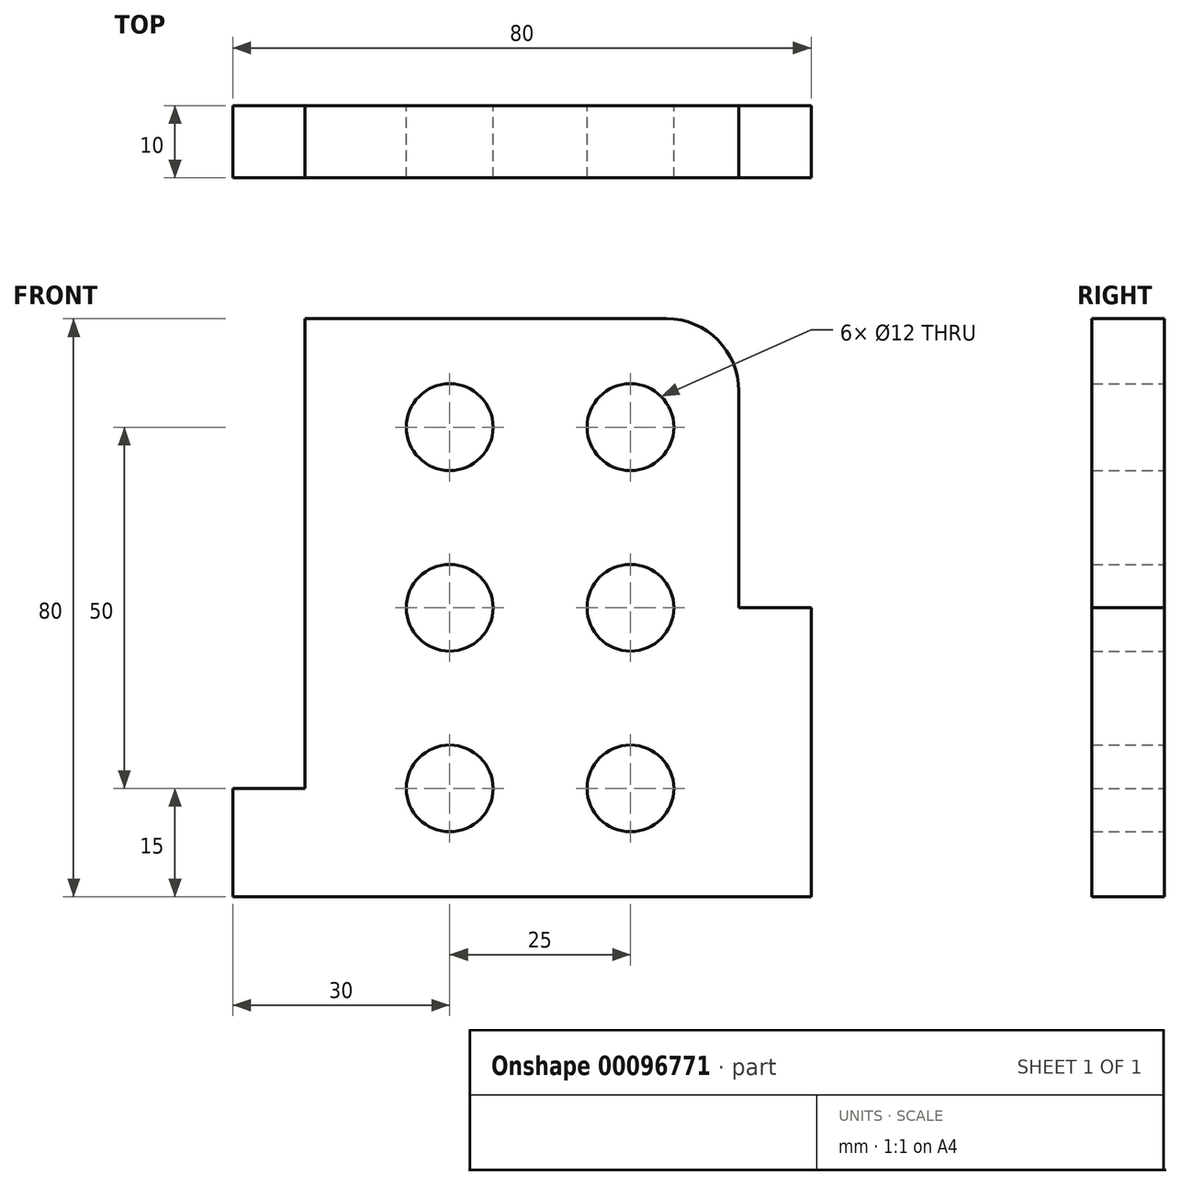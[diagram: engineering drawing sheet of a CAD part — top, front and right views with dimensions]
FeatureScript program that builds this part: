
annotation { "Feature Type Name" : "Feature", "Feature Type Description" : "" }
export const myFeature = defineFeature(function(context is Context, id is Id, definition is map)
    precondition{}
    {
        {
            var Q0;
            Q0=qCreatedBy(makeId("Front.planeOp"),FACE);
            var sketch = newSketch(context, id + "F0", { "sketchPlane" : qUnion([Q0])});
            skLineSegment(sketch, "E0", {"start": v(0, 0) * mm, "end": v(0, 15) * mm});
            skLineSegment(sketch, "E1", {"start": v(0, 15) * mm, "end": v(10, 15) * mm});
            skLineSegment(sketch, "E2", {"start": v(10, 15) * mm, "end": v(10, 80) * mm});
            skLineSegment(sketch, "E3", {"start": v(10, 80) * mm, "end": v(60, 80) * mm});
            skLineSegment(sketch, "E4", {"start": v(70, 70) * mm, "end": v(70, 40) * mm});
            skLineSegment(sketch, "E5", {"start": v(70, 40) * mm, "end": v(80, 40) * mm});
            skLineSegment(sketch, "E6", {"start": v(80, 40) * mm, "end": v(80, 0) * mm});
            skLineSegment(sketch, "E7", {"start": v(80, 0) * mm, "end": v(0, 0) * mm});
            skLineSegment(sketch, "E8", {"start": v(30, 80) * mm, "end": v(30, 0) * mm, "construction": true});
            skPoint(sketch, "E9.visualSharp", {"position": v(70, 80) * mm});
            skArc(sketch, "E9.filletArc", {"start": v(70, 70) * mm, "mid": v(67.07, 77.07) * mm, "end": v(60, 80) * mm});
            skLineSegment(sketch, "E10", {"start": v(10, 40) * mm, "end": v(70, 40) * mm, "construction": true});
            skLineSegment(sketch, "E11", {"start": v(10, 15) * mm, "end": v(80, 15) * mm, "construction": true});
            skLineSegment(sketch, "E12", {"start": v(10, 65) * mm, "end": v(70, 65) * mm, "construction": true});
            skLineSegment(sketch, "E13", {"start": v(55, 80) * mm, "end": v(55, 0) * mm, "construction": true});
            skCircle(sketch, "E14", {"center": v(30, 65) * mm, "radius": 6 * mm});
            skCircle(sketch, "E15", {"center": v(30, 40) * mm, "radius": 6 * mm});
            skCircle(sketch, "E16", {"center": v(30, 15) * mm, "radius": 6 * mm});
            skCircle(sketch, "E17", {"center": v(55, 40) * mm, "radius": 6 * mm});
            skPoint(sketch, "E17.perimeterSnap0", {"position": v(55, 40) * mm});
            skPoint(sketch, "E17.perimeterSnap1", {"position": v(45, 15) * mm});
            skCircle(sketch, "E18", {"center": v(55, 65) * mm, "radius": 6 * mm});
            skCircle(sketch, "E19", {"center": v(55, 15) * mm, "radius": 6 * mm});
            skSolve(sketch);
        }
        {
            var Q0;
            Q0 = qSketchRegion(id + "F0", true);
            extrude(context, id + "F1", {"entities" : qUnion([Q0]), "depth" : 10 * mm});
        }
    });
